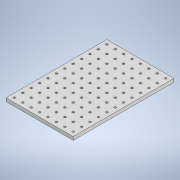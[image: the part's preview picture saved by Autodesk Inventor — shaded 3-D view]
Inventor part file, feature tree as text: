
AUTODESK INVENTOR PART (.ipt)
format: ipt  version: 2020 (Build 240168000, 168)  size: 192,000 bytes
history: native  units: mm
features: extrude x2, sketch x2, pattern_linear x1
ambient origin geometry x8: Origin, YZ Plane, XZ Plane, XY Plane, X Axis, Y Axis, Z Axis, Center Point
bodies: Solid1 (feature_tree)
feature tree (5):
  extrude  "Extrusion1"  Depth=10.0mm
  extrude  "Extrusion2"  Depth=300.0mm
  pattern_linear  "Rectangular Pattern1"  Spacing1=12.5mm  [1 undecoded]
  sketch  "Sketch1"  dims[d0=200.0mm d1=10.0mm]
  sketch  "Sketch2"  dims[d2=300.0mm d3=0.0mm d4=12.5mm d5=12.5mm d6=6.0mm d7=20.0mm d8=0.0mm d9=80.0mm d11=25.0mm d12=120.0mm d14=25.0mm]
note: 1 required parameter value undecoded (feature->parameter linkage not recoverable at this tier; creation-order binding heuristic only, values carry confidence <= 0.55)
